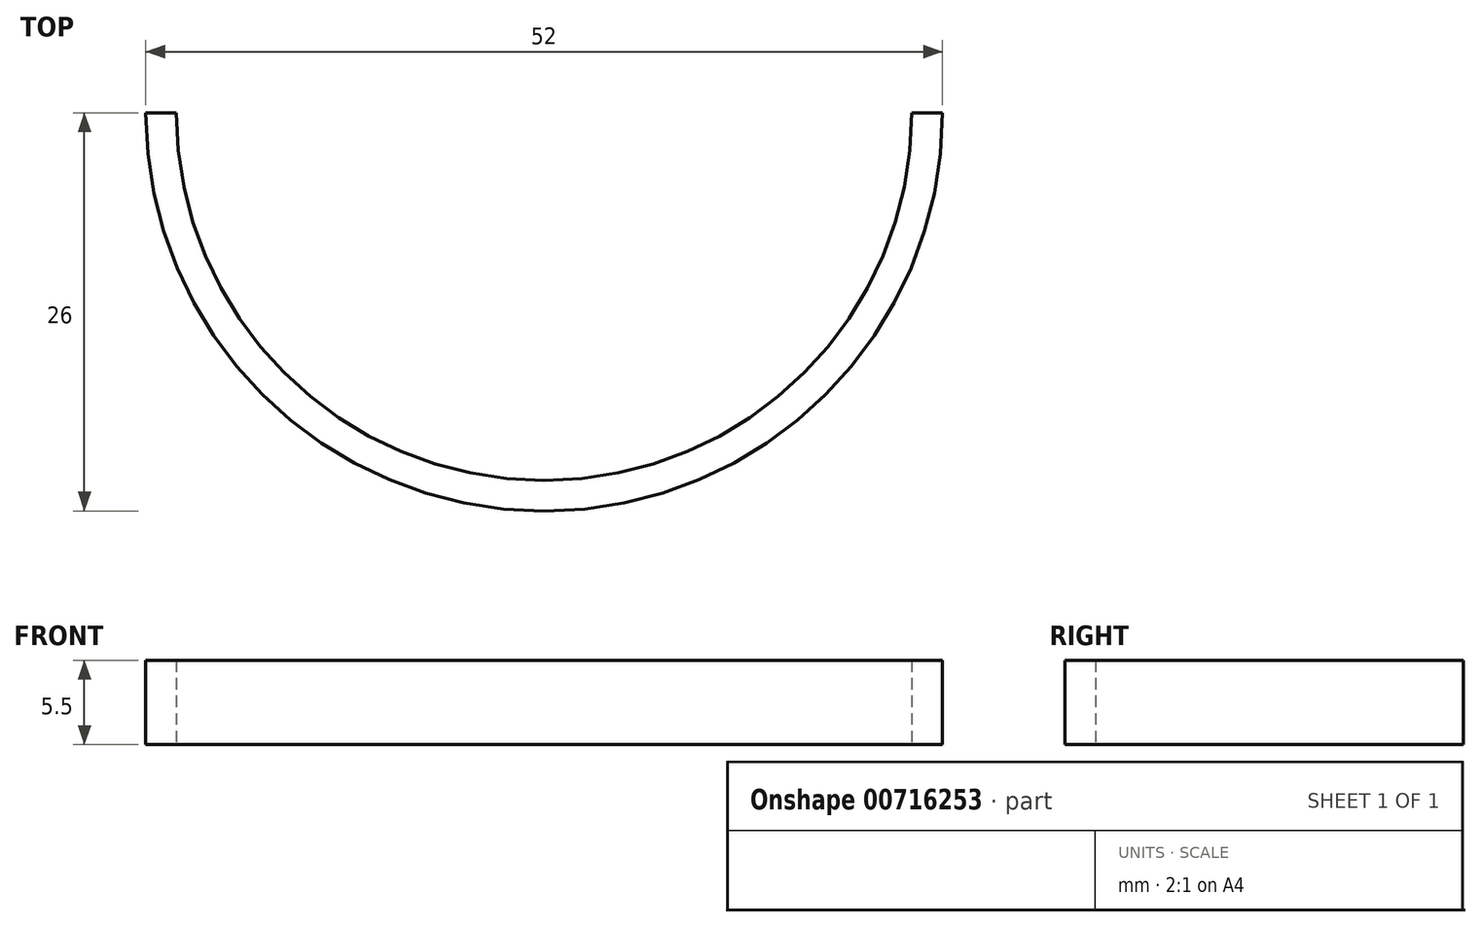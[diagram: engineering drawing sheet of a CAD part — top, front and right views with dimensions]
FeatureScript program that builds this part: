
annotation { "Feature Type Name" : "Feature", "Feature Type Description" : "" }
export const myFeature = defineFeature(function(context is Context, id is Id, definition is map)
    precondition{}
    {
        {
            var Q0;
            Q0=qCreatedBy(makeId("Top.planeOp"),FACE);
            var sketch = newSketch(context, id + "F0", { "sketchPlane" : qUnion([Q0])});
            skCircle(sketch, "E0", {"center": v(0, 0) * mm, "radius": 26 * mm});
            skCircle(sketch, "E1", {"center": v(0, 0) * mm, "radius": 24 * mm});
            skLineSegment(sketch, "E2", {"start": v(-26, 0) * mm, "end": v(26, 0) * mm});
            skSolve(sketch);
        }
        {
            var Q0;
            {var subQ0=sQuery(id+"F0.wireOp",EDGE,"E2");var subQ1=sQuery(id+"F0.wireOp",EDGE,"E0");var subQ2=makeQuery(id+"F0.imprint","INTERSECT",VERTEX,{"disambiguationData":[OD(0.0)],"derivedFrom":[subQ1,subQ0]});Q0=makeQuery(id+"F0.imprint","IMPRINT",FACE,{"disambiguationData":[TD([[makeQuery(id+"F0.imprint","IMPRINT",EDGE,{"disambiguationData":[TD([[subQ2,1.0]])],"derivedFrom":subQ1}),1.0]])]});}
            extrude(context, id + "F1", {"entities" : qUnion([Q0]), "depth" : 5.5 * mm, "offsetDistance" : 25 * mm});
        }
    });
